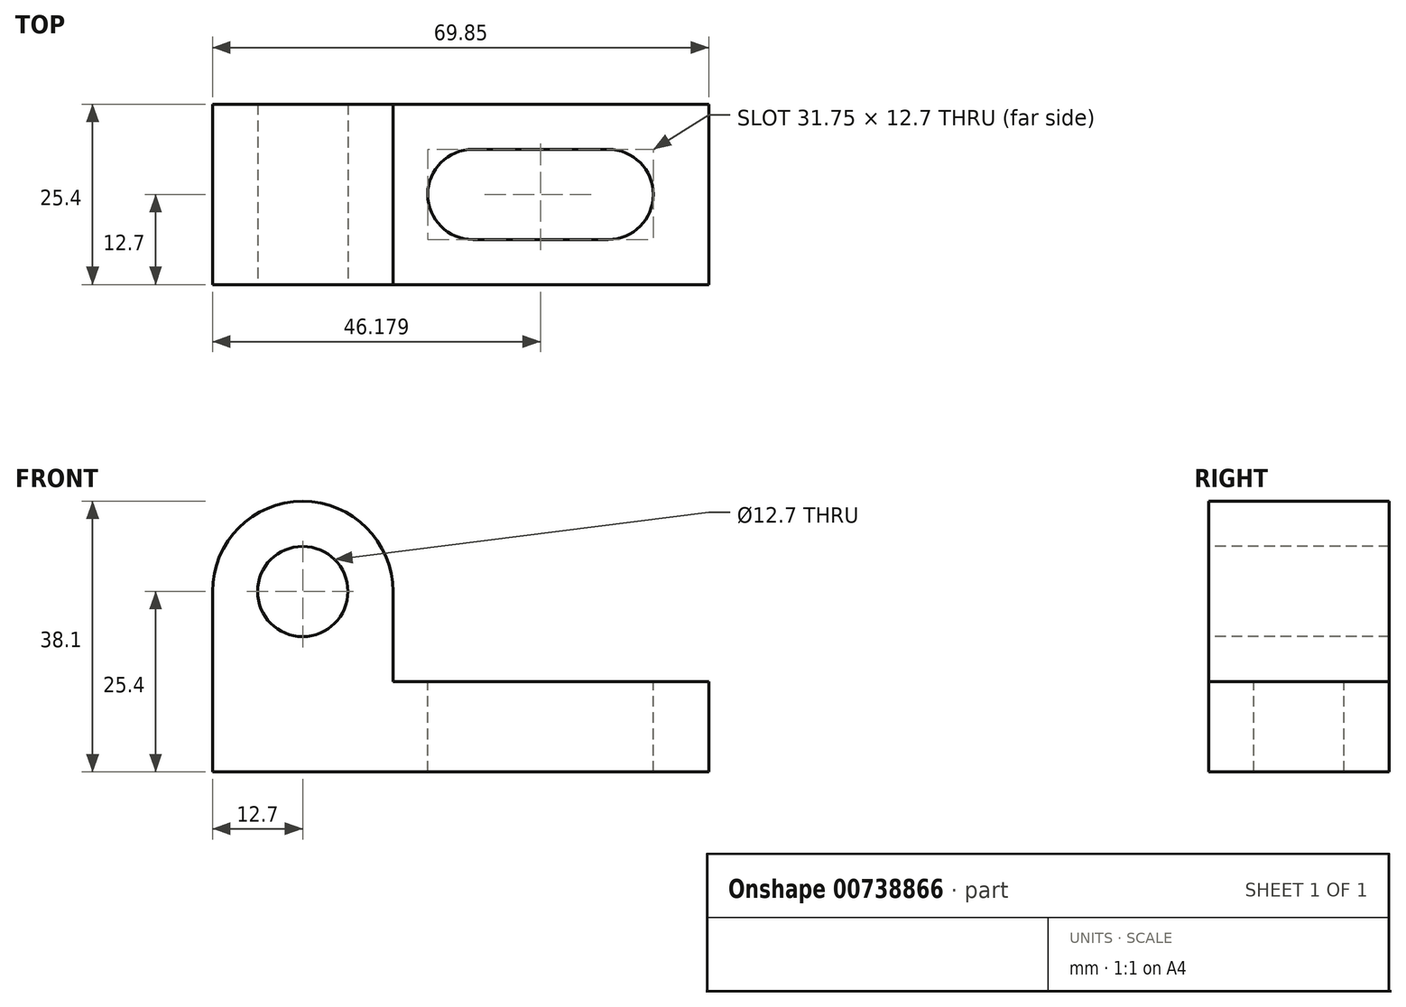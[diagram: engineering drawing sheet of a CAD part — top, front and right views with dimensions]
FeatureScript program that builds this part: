
annotation { "Feature Type Name" : "Feature", "Feature Type Description" : "" }
export const myFeature = defineFeature(function(context is Context, id is Id, definition is map)
    precondition{}
    {
        {
            var Q0;
            Q0=qCreatedBy(makeId("Front.planeOp"),FACE);
            var sketch = newSketch(context, id + "F0", { "sketchPlane" : qUnion([Q0])});
            skLineSegment(sketch, "E0.bottom", {"start": v(0, 0) * mm, "end": v(69.85, 0) * mm});
            skLineSegment(sketch, "E0.top", {"start": v(0, 38.1) * mm, "end": v(69.85, 38.1) * mm});
            skLineSegment(sketch, "E0.left", {"start": v(0, 0) * mm, "end": v(0, 38.1) * mm});
            skLineSegment(sketch, "E0.right", {"start": v(69.85, 0) * mm, "end": v(69.85, 38.1) * mm});
            skSolve(sketch);
        }
        {
            var Q0;
            Q0 = qSketchRegion(id + "F0", true);
            extrude(context, id + "F1", {"entities" : qUnion([Q0]), "depth" : 25.4 * mm, "offsetDistance" : 25.4 * mm});
        }
        {
            var Q0;
            Q0=makeQuery(id+"F1.opExtrude","CAP_FACE",FACE,{"disambiguationData":[OSD([sQuery(id+"F0.wireOp",EDGE,"E0.bottom"),sQuery(id+"F0.wireOp",EDGE,"E0.top"),sQuery(id+"F0.wireOp",EDGE,"E0.left"),sQuery(id+"F0.wireOp",EDGE,"E0.right")])],"isStart":false});
            var sketch = newSketch(context, id + "F2", { "sketchPlane" : qUnion([Q0])});
            skLineSegment(sketch, "E1", {"start": v(25.4, 38.1) * mm, "end": v(25.4, 12.7) * mm});
            skLineSegment(sketch, "E2", {"start": v(25.4, 12.7) * mm, "end": v(69.85, 12.7) * mm});
            skSolve(sketch);
        }
        {
            var Q0;
            {var subQ0=sQuery(id+"F2.wireOp",EDGE,"E1");Q0=makeQuery(id+"F2.imprint","IMPRINT",FACE,{"disambiguationData":[TD([[makeQuery(id+"F2.imprint","IMPRINT",EDGE,{"derivedFrom":subQ0}),1.0]])]});}
            extrude(context, id + "F3", {"entities" : qUnion([Q0]), "operationType" : NewBodyOperationType.REMOVE, "oppositeDirection" : true, "depth" : 25.4 * mm, "offsetDistance" : 25.4 * mm});
        }
        {
            var Q0;
            Q0=makeQuery(id+"F1.opExtrude","CAP_FACE",FACE,{"disambiguationData":[OSD([sQuery(id+"F0.wireOp",EDGE,"E0.bottom"),sQuery(id+"F0.wireOp",EDGE,"E0.top"),sQuery(id+"F0.wireOp",EDGE,"E0.left"),sQuery(id+"F0.wireOp",EDGE,"E0.right")])],"isStart":false});
            var sketch = newSketch(context, id + "F4", { "sketchPlane" : qUnion([Q0])});
            skCircle(sketch, "E3", {"center": v(12.7, 25.4) * mm, "radius": 6.35 * mm});
            skArc(sketch, "E4", {"start": v(25.4, 25.4) * mm, "mid": v(12.7, 38.1) * mm, "end": v(0, 25.4) * mm});
            skSolve(sketch);
        }
        {
            var Q0;
            Q0 = qSketchRegion(id + "F4", true);
            var Q1;
            {var subQ0=sQuery(id+"F4.wireOp",EDGE,"E4");var subQ1=makeQuery(id+"F3.boolean.opBoolean","COPY",EDGE,{"derivedFrom":makeQuery(id+"F3.opExtrude","CAP_EDGE",EDGE,{"disambiguationData":[OSD([sQuery(id+"F2.wireOp",EDGE,"E1")])],"isStart":true})});var subQ2=makeQuery(id+"F4.imprint","INTERSECT",VERTEX,{"derivedFrom":[subQ1,subQ0]});Q1=makeQuery(id+"F4.imprint","IMPRINT",FACE,{"disambiguationData":[TD([[makeQuery(id+"F4.imprint","IMPRINT",EDGE,{"disambiguationData":[TD([[subQ2,-1.0]])],"derivedFrom":subQ0}),-1.0]])]});}
            var Q2;
            {var subQ0=sQuery(id+"F4.wireOp",EDGE,"E4");var subQ1=makeQuery(id+"F1.opExtrude","CAP_EDGE",EDGE,{"disambiguationData":[OSD([sQuery(id+"F0.wireOp",EDGE,"E0.left")])],"isStart":false});var subQ2=makeQuery(id+"F4.imprint","INTERSECT",VERTEX,{"derivedFrom":[subQ1,subQ0]});Q2=makeQuery(id+"F4.imprint","IMPRINT",FACE,{"disambiguationData":[TD([[makeQuery(id+"F4.imprint","IMPRINT",EDGE,{"disambiguationData":[TD([[subQ2,1.0]])],"derivedFrom":subQ0}),-1.0]])]});}
            extrude(context, id + "F5", {"entities" : qUnion([Q0, Q1, Q2]), "operationType" : NewBodyOperationType.REMOVE, "oppositeDirection" : true, "depth" : 25.4 * mm, "offsetDistance" : 25.4 * mm});
        }
        {
            var Q0;
            Q0=makeQuery(id+"F3.boolean.opBoolean","COPY",FACE,{"derivedFrom":makeQuery(id+"F3.opExtrude","SWEPT_FACE",FACE,{"disambiguationData":[OSD([sQuery(id+"F2.wireOp",EDGE,"E2")])]})});
            var sketch = newSketch(context, id + "F6", { "sketchPlane" : qUnion([Q0])});
            skCircle(sketch, "E5", {"center": v(36.65, -12.7) * mm, "radius": 6.35 * mm});
            skCircle(sketch, "E6", {"center": v(55.7, -12.7) * mm, "radius": 6.35 * mm});
            skLineSegment(sketch, "E7", {"start": v(36.65, -6.35) * mm, "end": v(55.7, -6.35) * mm});
            skLineSegment(sketch, "E8", {"start": v(36.65, -19.05) * mm, "end": v(55.7, -19.05) * mm});
            skArc(sketch, "E9", {"start": v(55.7, -25.4) * mm, "mid": v(69.85, -12.7) * mm, "end": v(55.7, 0) * mm});
            skSolve(sketch);
        }
        {
            var Q0;
            {var subQ0=sQuery(id+"F6.wireOp",EDGE,"E6");var subQ1=makeQuery(id+"F6.imprint","INTERSECT",VERTEX,{"derivedFrom":[subQ0,sQuery(id+"F6.wireOp",EDGE,"E7")]});Q0=makeQuery(id+"F6.imprint","IMPRINT",FACE,{"disambiguationData":[TD([[makeQuery(id+"F6.imprint","IMPRINT",EDGE,{"disambiguationData":[TD([[subQ1,-1.0]])],"derivedFrom":subQ0}),1.0]])]});}
            var Q1;
            {var subQ0=sQuery(id+"F6.wireOp",EDGE,"E7");Q1=makeQuery(id+"F6.imprint","IMPRINT",FACE,{"disambiguationData":[TD([[makeQuery(id+"F6.imprint","IMPRINT",EDGE,{"derivedFrom":subQ0}),-1.0]])]});}
            var Q2;
            {var subQ0=sQuery(id+"F6.wireOp",EDGE,"E5");var subQ1=makeQuery(id+"F6.imprint","INTERSECT",VERTEX,{"derivedFrom":[subQ0,sQuery(id+"F6.wireOp",EDGE,"E7")]});Q2=makeQuery(id+"F6.imprint","IMPRINT",FACE,{"disambiguationData":[TD([[makeQuery(id+"F6.imprint","IMPRINT",EDGE,{"disambiguationData":[TD([[subQ1,-1.0]])],"derivedFrom":subQ0}),1.0]])]});}
            var Q3;
            {var subQ0=sQuery(id+"F6.wireOp",EDGE,"E9");var subQ1=sQuery(id+"F2.wireOp",EDGE,"E2");var subQ4=makeQuery(id+"F3.boolean.opBoolean","COPY",EDGE,{"derivedFrom":makeQuery(id+"F3.opExtrude","CAP_EDGE",EDGE,{"disambiguationData":[OSD([subQ1])],"isStart":false})});var subQ5=makeQuery(id+"F6.imprint","INTERSECT",VERTEX,{"disambiguationData":[OD(1.0)],"derivedFrom":[subQ4,subQ0]});Q3=makeQuery(id+"F6.imprint","IMPRINT",FACE,{"disambiguationData":[TD([[makeQuery(id+"F6.imprint","IMPRINT",EDGE,{"disambiguationData":[TD([[subQ5,1.0]])],"derivedFrom":subQ0}),-1.0]])]});}
            var Q4;
            {var subQ0=sQuery(id+"F6.wireOp",EDGE,"E9");var subQ1=sQuery(id+"F2.wireOp",EDGE,"E2");var subQ2=makeQuery(id+"F3.boolean.opBoolean","COPY",EDGE,{"derivedFrom":makeQuery(id+"F3.opExtrude","CAP_EDGE",EDGE,{"disambiguationData":[OSD([subQ1])],"isStart":true})});var subQ3=makeQuery(id+"F6.imprint","INTERSECT",VERTEX,{"disambiguationData":[OD(1.0)],"derivedFrom":[subQ2,subQ0]});Q4=makeQuery(id+"F6.imprint","IMPRINT",FACE,{"disambiguationData":[TD([[makeQuery(id+"F6.imprint","IMPRINT",EDGE,{"disambiguationData":[TD([[subQ3,-1.0]])],"derivedFrom":subQ0}),-1.0]])]});}
            extrude(context, id + "F7", {"entities" : qUnion([Q0, Q1, Q2, Q3, Q4]), "operationType" : NewBodyOperationType.REMOVE, "oppositeDirection" : true, "depth" : 25.4 * mm, "offsetDistance" : 25.4 * mm});
        }
    });
